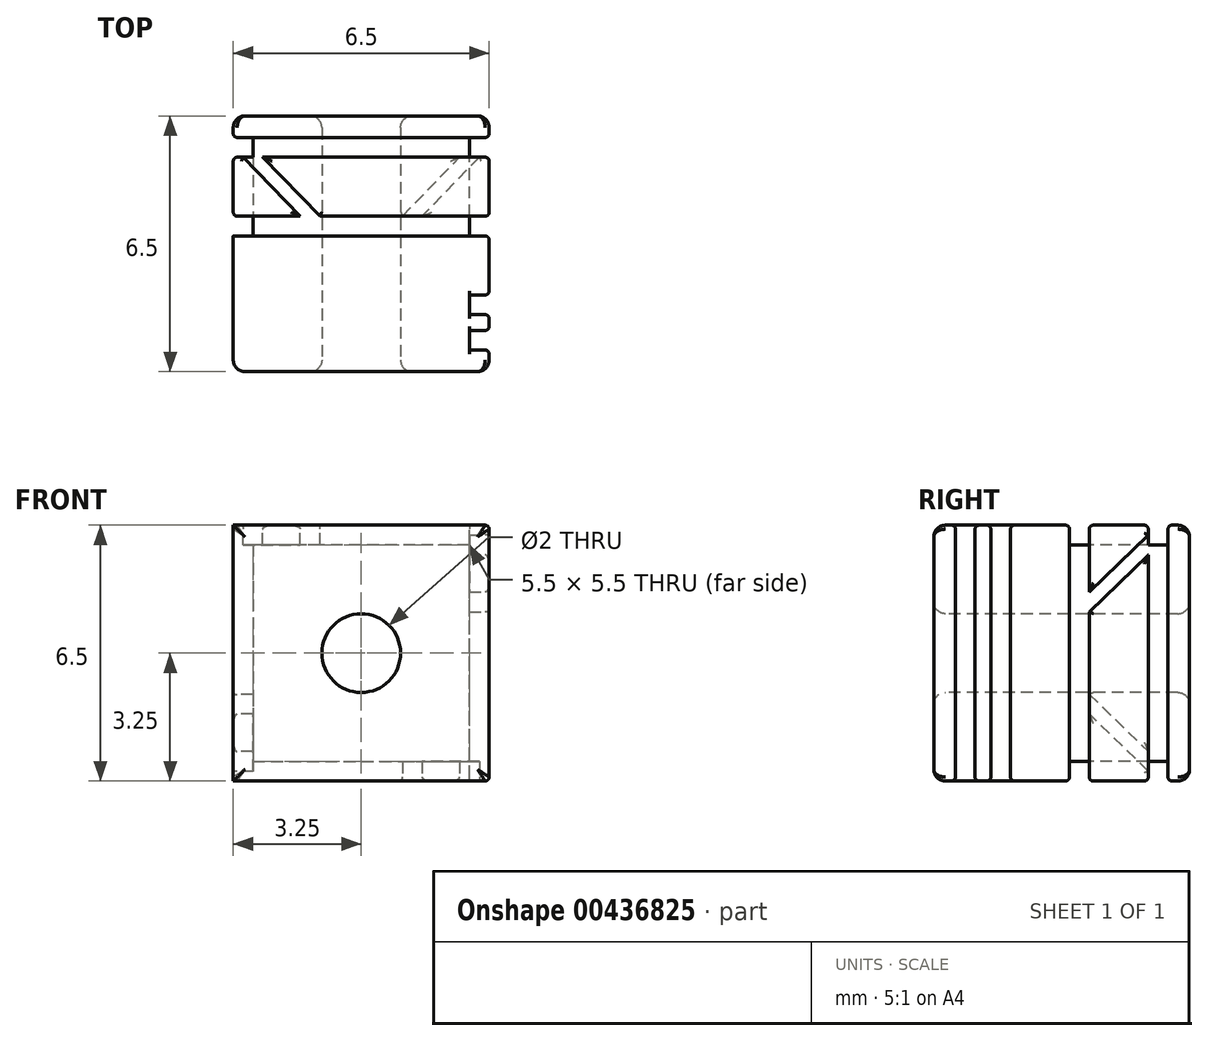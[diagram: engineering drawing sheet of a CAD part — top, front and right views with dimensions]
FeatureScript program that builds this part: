
annotation { "Feature Type Name" : "Feature", "Feature Type Description" : "" }
export const myFeature = defineFeature(function(context is Context, id is Id, definition is map)
    precondition{}
    {
        {
            var Q0;
            Q0=qCreatedBy(makeId("Front.planeOp"),FACE);
            var sketch = newSketch(context, id + "F0", { "sketchPlane" : qUnion([Q0])});
            skLineSegment(sketch, "E0.bottom", {"start": v(0, 0) * mm, "end": v(6.5, 0) * mm});
            skLineSegment(sketch, "E0.top", {"start": v(0, -6.5) * mm, "end": v(6.5, -6.5) * mm});
            skLineSegment(sketch, "E0.left", {"start": v(0, 0) * mm, "end": v(0, -6.5) * mm});
            skLineSegment(sketch, "E0.right", {"start": v(6.5, 0) * mm, "end": v(6.5, -6.5) * mm});
            skSolve(sketch);
        }
        {
            var Q0;
            Q0=makeQuery(id+"F0.imprint","IMPRINT",FACE,{"disambiguationData":[TD([[makeQuery(id+"F0.imprint","IMPRINT",EDGE,{"derivedFrom":sQuery(id+"F0.wireOp",EDGE,"E0.bottom")}),-1.0]])]});
            extrude(context, id + "F1", {"entities" : qUnion([Q0]), "depth" : 6.5 * mm});
        }
        {
            var Q0;
            Q0=makeQuery(id+"F1.opExtrude","CAP_FACE",FACE,{"disambiguationData":[OSD([sQuery(id+"F0.wireOp",EDGE,"E0.bottom"),sQuery(id+"F0.wireOp",EDGE,"E0.top"),sQuery(id+"F0.wireOp",EDGE,"E0.left"),sQuery(id+"F0.wireOp",EDGE,"E0.right")])],"isStart":false});
            var sketch = newSketch(context, id + "F2", { "sketchPlane" : qUnion([Q0])});
            skCircle(sketch, "E1", {"center": v(3.25, -3.25) * mm, "radius": 1 * mm});
            skPoint(sketch, "E1.centerSnap0", {"position": v(3.25, -6.5) * mm});
            skPoint(sketch, "E1.centerSnap1", {"position": v(0, -3.25) * mm});
            skSolve(sketch);
        }
        {
            var Q0;
            Q0=makeQuery(id+"F2.imprint","IMPRINT",FACE,{"disambiguationData":[TD([[makeQuery(id+"F2.imprint","IMPRINT",EDGE,{"derivedFrom":sQuery(id+"F2.wireOp",EDGE,"E1")}),1.0]])]});
            extrude(context, id + "F3", {"entities" : qUnion([Q0]), "operationType" : NewBodyOperationType.REMOVE, "oppositeDirection" : true, "depth" : 25 * mm});
        }
        {
            var Q0;
            Q0=makeQuery(id+"F1.opExtrude","SWEPT_FACE",FACE,{"disambiguationData":[OSD([sQuery(id+"F0.wireOp",EDGE,"E0.right")])]});
            var sketch = newSketch(context, id + "F4", { "sketchPlane" : qUnion([Q0])});
            skLineSegment(sketch, "E2", {"start": v(-5.95, -6.5) * mm, "end": v(-5.95, 0) * mm});
            skLineSegment(sketch, "E3", {"start": v(-0.55, -6.5) * mm, "end": v(-0.55, 0) * mm});
            skLineSegment(sketch, "E4.bottom", {"start": v(-5.45, -6.5) * mm, "end": v(-5.05, -6.5) * mm});
            skLineSegment(sketch, "E4.top", {"start": v(-5.45, 0) * mm, "end": v(-5.05, 0) * mm});
            skLineSegment(sketch, "E4.left", {"start": v(-5.45, -6.5) * mm, "end": v(-5.45, 0) * mm});
            skLineSegment(sketch, "E4.right", {"start": v(-5.05, -6.5) * mm, "end": v(-5.05, 0) * mm});
            skLineSegment(sketch, "E5.bottom", {"start": v(-4.55, -6.5) * mm, "end": v(-3.05, -6.5) * mm});
            skLineSegment(sketch, "E5.top", {"start": v(-4.55, 0) * mm, "end": v(-3.05, 0) * mm});
            skLineSegment(sketch, "E5.left", {"start": v(-4.55, -6.5) * mm, "end": v(-4.55, 0) * mm});
            skLineSegment(sketch, "E5.right", {"start": v(-3.05, -6.5) * mm, "end": v(-3.05, 0) * mm});
            skLineSegment(sketch, "E6.bottom", {"start": v(-2.55, -6.5) * mm, "end": v(-1.05, -6.5) * mm});
            skLineSegment(sketch, "E6.top", {"start": v(-2.55, 0) * mm, "end": v(-1.05, 0) * mm});
            skLineSegment(sketch, "E6.left", {"start": v(-2.55, -6.5) * mm, "end": v(-2.55, -2.2) * mm});
            skLineSegment(sketch, "E6.right", {"start": v(-1.05, -6.5) * mm, "end": v(-1.05, -0.75) * mm});
            skLineSegment(sketch, "E7", {"start": v(-1.05, -0.25) * mm, "end": v(-2.55, -1.7) * mm});
            skLineSegment(sketch, "E8", {"start": v(-2.55, -2.2) * mm, "end": v(-1.05, -0.75) * mm});
            skLineSegment(sketch, "E9.trimOffspring", {"start": v(-2.55, -1.7) * mm, "end": v(-2.55, 0) * mm});
            skLineSegment(sketch, "E10.trimOffspring", {"start": v(-1.05, -0.25) * mm, "end": v(-1.05, 0) * mm});
            skSolve(sketch);
        }
        {
            var Q0;
            {var subQ0=sQuery(id+"F4.wireOp",EDGE,"E2");Q0=makeQuery(id+"F4.imprint","IMPRINT",FACE,{"disambiguationData":[TD([[makeQuery(id+"F4.imprint","IMPRINT",EDGE,{"derivedFrom":subQ0}),-1.0]])]});}
            var Q1;
            {var subQ0=sQuery(id+"F4.wireOp",EDGE,"E4.right");Q1=makeQuery(id+"F4.imprint","IMPRINT",FACE,{"disambiguationData":[TD([[makeQuery(id+"F4.imprint","IMPRINT",EDGE,{"derivedFrom":subQ0}),-1.0]])]});}
            var Q2;
            {var subQ6=sQuery(id+"F4.wireOp",EDGE,"E3");Q2=makeQuery(id+"F4.imprint","IMPRINT",FACE,{"disambiguationData":[TD([[makeQuery(id+"F4.imprint","IMPRINT",EDGE,{"derivedFrom":subQ6}),1.0]])]});}
            extrude(context, id + "F5", {"entities" : qUnion([Q0, Q1, Q2]), "operationType" : NewBodyOperationType.REMOVE, "oppositeDirection" : true, "depth" : 0.5 * mm, "offsetDistance" : 25 * mm});
        }
        {
            var Q0;
            Q0=makeQuery(id+"F1.opExtrude","SWEPT_FACE",FACE,{"disambiguationData":[OSD([sQuery(id+"F0.wireOp",EDGE,"E0.bottom")])]});
            var sketch = newSketch(context, id + "F6", { "sketchPlane" : qUnion([Q0])});
            skLineSegment(sketch, "E11", {"start": v(6.5, -5.95) * mm, "end": v(0, -5.95) * mm});
            skLineSegment(sketch, "E12", {"start": v(6.5, -0.55) * mm, "end": v(0, -0.55) * mm});
            skLineSegment(sketch, "E13.bottom", {"start": v(6.5, -5.45) * mm, "end": v(6.5, -5.05) * mm});
            skLineSegment(sketch, "E13.top", {"start": v(0, -5.45) * mm, "end": v(0, -5.05) * mm});
            skLineSegment(sketch, "E13.left", {"start": v(6.5, -5.45) * mm, "end": v(0, -5.45) * mm});
            skLineSegment(sketch, "E13.right", {"start": v(6.5, -5.05) * mm, "end": v(0, -5.05) * mm});
            skLineSegment(sketch, "E14.bottom", {"start": v(6.5, -4.55) * mm, "end": v(6.5, -3.05) * mm});
            skLineSegment(sketch, "E14.top", {"start": v(0, -4.55) * mm, "end": v(0, -3.05) * mm});
            skLineSegment(sketch, "E14.left", {"start": v(6.5, -4.55) * mm, "end": v(0, -4.55) * mm});
            skLineSegment(sketch, "E14.right", {"start": v(6.5, -3.05) * mm, "end": v(0, -3.05) * mm});
            skLineSegment(sketch, "E15.bottom", {"start": v(6.5, -2.55) * mm, "end": v(6.5, -1.05) * mm});
            skLineSegment(sketch, "E15.top", {"start": v(0, -2.55) * mm, "end": v(0, -1.05) * mm});
            skLineSegment(sketch, "E15.left", {"start": v(6.5, -2.55) * mm, "end": v(2.2, -2.55) * mm});
            skLineSegment(sketch, "E15.right", {"start": v(6.5, -1.05) * mm, "end": v(0.75, -1.05) * mm});
            skLineSegment(sketch, "E16", {"start": v(0.25, -1.05) * mm, "end": v(1.7, -2.55) * mm});
            skLineSegment(sketch, "E17", {"start": v(2.2, -2.55) * mm, "end": v(0.75, -1.05) * mm});
            skLineSegment(sketch, "E18.trimOffspring", {"start": v(1.7, -2.55) * mm, "end": v(0, -2.55) * mm});
            skLineSegment(sketch, "E19.trimOffspring", {"start": v(0.25, -1.05) * mm, "end": v(0, -1.05) * mm});
            skSolve(sketch);
        }
        {
            var Q0;
            {var subQ1=sQuery(id+"F0.wireOp",EDGE,"E0.right");var subQ2=sQuery(id+"F0.wireOp",EDGE,"E0.bottom");var subQ3=makeQuery(id+"F1.opExtrude","SWEPT_EDGE",EDGE,{"disambiguationData":[OSD([subQ2,subQ1])]});var subQ4=makeQuery(id+"F5.boolean.opBoolean","COPY",EDGE,{"derivedFrom":makeQuery(id+"F5.opExtrude","CAP_EDGE",EDGE,{"disambiguationData":[OSD([subQ2,subQ1]),TDD([makeQuery(id+"F4.imprint","IMPRINT",EDGE,{"disambiguationData":[TD([[makeQuery(id+"F4.imprint","INTERSECT",VERTEX,{"derivedFrom":[subQ3,sQuery(id+"F4.wireOp",EDGE,"E2")]}),-1.0]])],"derivedFrom":subQ3})])],"isStart":false})});Q0=makeQuery(id+"F6.imprint","IMPRINT",FACE,{"disambiguationData":[TD([[makeQuery(id+"F6.imprint","IMPRINT",EDGE,{"derivedFrom":subQ4}),1.0]])]});}
            var Q1;
            {var subQ1=sQuery(id+"F0.wireOp",EDGE,"E0.right");var subQ2=sQuery(id+"F0.wireOp",EDGE,"E0.bottom");var subQ3=makeQuery(id+"F1.opExtrude","SWEPT_EDGE",EDGE,{"disambiguationData":[OSD([subQ2,subQ1])]});var subQ4=makeQuery(id+"F5.boolean.opBoolean","COPY",EDGE,{"derivedFrom":makeQuery(id+"F5.opExtrude","CAP_EDGE",EDGE,{"disambiguationData":[OSD([subQ2,subQ1]),TDD([makeQuery(id+"F4.imprint","IMPRINT",EDGE,{"disambiguationData":[TD([[makeQuery(id+"F4.imprint","INTERSECT",VERTEX,{"derivedFrom":[subQ3,sQuery(id+"F4.wireOp",EDGE,"E4.top"),sQuery(id+"F4.wireOp",EDGE,"E4.right")]}),-1.0]])],"derivedFrom":subQ3})])],"isStart":false})});Q1=makeQuery(id+"F6.imprint","IMPRINT",FACE,{"disambiguationData":[TD([[makeQuery(id+"F6.imprint","IMPRINT",EDGE,{"derivedFrom":subQ4}),1.0]])]});}
            var Q2;
            Q2=makeQuery(id+"F6.imprint","IMPRINT",FACE,{"disambiguationData":[TD([[makeQuery(id+"F6.imprint","IMPRINT",EDGE,{"derivedFrom":sQuery(id+"F6.wireOp",EDGE,"E16")}),1.0]])]});
            extrude(context, id + "F7", {"entities" : qUnion([Q0, Q1, Q2]), "operationType" : NewBodyOperationType.REMOVE, "oppositeDirection" : true, "depth" : 0.5 * mm, "offsetDistance" : 25 * mm});
        }
        {
            var Q0;
            Q0=makeQuery(id+"F1.opExtrude","SWEPT_FACE",FACE,{"disambiguationData":[OSD([sQuery(id+"F0.wireOp",EDGE,"E0.left")])]});
            var sketch = newSketch(context, id + "F8", { "sketchPlane" : qUnion([Q0])});
            skLineSegment(sketch, "E20", {"start": v(5.95, 0) * mm, "end": v(5.95, -6.5) * mm});
            skLineSegment(sketch, "E21", {"start": v(0.55, 0) * mm, "end": v(0.55, -6.5) * mm});
            skLineSegment(sketch, "E22.bottom", {"start": v(5.45, 0) * mm, "end": v(5.05, 0) * mm});
            skLineSegment(sketch, "E22.top", {"start": v(5.45, -6.5) * mm, "end": v(5.05, -6.5) * mm});
            skLineSegment(sketch, "E22.left", {"start": v(5.45, 0) * mm, "end": v(5.45, -6.5) * mm});
            skLineSegment(sketch, "E22.right", {"start": v(5.05, 0) * mm, "end": v(5.05, -6.5) * mm});
            skLineSegment(sketch, "E23.bottom", {"start": v(4.55, 0) * mm, "end": v(3.05, 0) * mm});
            skLineSegment(sketch, "E23.top", {"start": v(4.55, -6.5) * mm, "end": v(3.05, -6.5) * mm});
            skLineSegment(sketch, "E23.left", {"start": v(4.55, 0) * mm, "end": v(4.55, -6.5) * mm});
            skLineSegment(sketch, "E23.right", {"start": v(3.05, 0) * mm, "end": v(3.05, -6.5) * mm});
            skLineSegment(sketch, "E24.bottom", {"start": v(2.55, 0) * mm, "end": v(1.05, 0) * mm});
            skLineSegment(sketch, "E24.top", {"start": v(2.55, -6.5) * mm, "end": v(1.05, -6.5) * mm});
            skLineSegment(sketch, "E24.left", {"start": v(2.55, 0) * mm, "end": v(2.55, -4.3) * mm});
            skLineSegment(sketch, "E24.right", {"start": v(1.05, 0) * mm, "end": v(1.05, -5.75) * mm});
            skLineSegment(sketch, "E25", {"start": v(1.05, -6.25) * mm, "end": v(2.55, -4.8) * mm});
            skLineSegment(sketch, "E26", {"start": v(2.55, -4.3) * mm, "end": v(1.05, -5.75) * mm});
            skLineSegment(sketch, "E27.trimOffspring", {"start": v(2.55, -4.8) * mm, "end": v(2.55, -6.5) * mm});
            skLineSegment(sketch, "E28.trimOffspring", {"start": v(1.05, -6.25) * mm, "end": v(1.05, -6.5) * mm});
            skSolve(sketch);
        }
        {
            var Q0;
            {var subQ1=sQuery(id+"F0.wireOp",EDGE,"E0.left");var subQ2=sQuery(id+"F0.wireOp",EDGE,"E0.bottom");var subQ3=makeQuery(id+"F1.opExtrude","SWEPT_EDGE",EDGE,{"disambiguationData":[OSD([subQ2,subQ1])]});var subQ4=makeQuery(id+"F7.boolean.opBoolean","COPY",EDGE,{"derivedFrom":makeQuery(id+"F7.opExtrude","CAP_EDGE",EDGE,{"disambiguationData":[OSD([subQ2,subQ1]),TDD([makeQuery(id+"F6.imprint","IMPRINT",EDGE,{"disambiguationData":[TD([[makeQuery(id+"F6.imprint","INTERSECT",VERTEX,{"derivedFrom":[subQ3,sQuery(id+"F6.wireOp",EDGE,"E11")]}),-1.0]])],"derivedFrom":subQ3})])],"isStart":false})});Q0=makeQuery(id+"F8.imprint","IMPRINT",FACE,{"disambiguationData":[TD([[makeQuery(id+"F8.imprint","IMPRINT",EDGE,{"derivedFrom":subQ4}),1.0]])]});}
            var Q1;
            {var subQ1=sQuery(id+"F0.wireOp",EDGE,"E0.left");var subQ2=sQuery(id+"F0.wireOp",EDGE,"E0.bottom");var subQ3=makeQuery(id+"F1.opExtrude","SWEPT_EDGE",EDGE,{"disambiguationData":[OSD([subQ2,subQ1])]});var subQ4=makeQuery(id+"F7.boolean.opBoolean","COPY",EDGE,{"derivedFrom":makeQuery(id+"F7.opExtrude","CAP_EDGE",EDGE,{"disambiguationData":[OSD([subQ2,subQ1]),TDD([makeQuery(id+"F6.imprint","IMPRINT",EDGE,{"disambiguationData":[TD([[makeQuery(id+"F6.imprint","INTERSECT",VERTEX,{"derivedFrom":[subQ3,sQuery(id+"F6.wireOp",EDGE,"E13.top"),sQuery(id+"F6.wireOp",EDGE,"E13.right")]}),-1.0]])],"derivedFrom":subQ3})])],"isStart":false})});Q1=makeQuery(id+"F8.imprint","IMPRINT",FACE,{"disambiguationData":[TD([[makeQuery(id+"F8.imprint","IMPRINT",EDGE,{"derivedFrom":subQ4}),1.0]])]});}
            var Q2;
            Q2=makeQuery(id+"F8.imprint","IMPRINT",FACE,{"disambiguationData":[TD([[makeQuery(id+"F8.imprint","IMPRINT",EDGE,{"derivedFrom":sQuery(id+"F8.wireOp",EDGE,"E25")}),1.0]])]});
            extrude(context, id + "F9", {"entities" : qUnion([Q0, Q1, Q2]), "operationType" : NewBodyOperationType.REMOVE, "oppositeDirection" : true, "depth" : 0.5 * mm, "offsetDistance" : 25 * mm});
        }
        {
            var Q0;
            Q0=makeQuery(id+"F1.opExtrude","SWEPT_FACE",FACE,{"disambiguationData":[OSD([sQuery(id+"F0.wireOp",EDGE,"E0.top")])]});
            var sketch = newSketch(context, id + "F10", { "sketchPlane" : qUnion([Q0])});
            skLineSegment(sketch, "E29", {"start": v(0, 5.95) * mm, "end": v(6.5, 5.95) * mm});
            skLineSegment(sketch, "E30", {"start": v(0, 0.55) * mm, "end": v(6.5, 0.55) * mm});
            skLineSegment(sketch, "E31.bottom", {"start": v(0, 5.45) * mm, "end": v(0, 5.05) * mm});
            skLineSegment(sketch, "E31.top", {"start": v(6.5, 5.45) * mm, "end": v(6.5, 5.05) * mm});
            skLineSegment(sketch, "E31.left", {"start": v(0, 5.45) * mm, "end": v(6.5, 5.45) * mm});
            skLineSegment(sketch, "E31.right", {"start": v(0, 5.05) * mm, "end": v(6.5, 5.05) * mm});
            skLineSegment(sketch, "E32.bottom", {"start": v(0, 4.55) * mm, "end": v(0, 3.05) * mm});
            skLineSegment(sketch, "E32.top", {"start": v(6.5, 4.55) * mm, "end": v(6.5, 3.05) * mm});
            skLineSegment(sketch, "E32.left", {"start": v(0, 4.55) * mm, "end": v(6.5, 4.55) * mm});
            skLineSegment(sketch, "E32.right", {"start": v(0, 3.05) * mm, "end": v(6.5, 3.05) * mm});
            skLineSegment(sketch, "E33.bottom", {"start": v(0, 2.55) * mm, "end": v(0, 1.05) * mm});
            skLineSegment(sketch, "E33.top", {"start": v(6.5, 2.55) * mm, "end": v(6.5, 1.05) * mm});
            skLineSegment(sketch, "E33.left", {"start": v(0, 2.55) * mm, "end": v(4.3, 2.55) * mm});
            skLineSegment(sketch, "E33.right", {"start": v(0, 1.05) * mm, "end": v(5.75, 1.05) * mm});
            skLineSegment(sketch, "E34", {"start": v(6.25, 1.05) * mm, "end": v(4.8, 2.55) * mm});
            skLineSegment(sketch, "E35", {"start": v(4.3, 2.55) * mm, "end": v(5.75, 1.05) * mm});
            skLineSegment(sketch, "E36.trimOffspring", {"start": v(4.8, 2.55) * mm, "end": v(6.5, 2.55) * mm});
            skLineSegment(sketch, "E37.trimOffspring", {"start": v(6.25, 1.05) * mm, "end": v(6.5, 1.05) * mm});
            skSolve(sketch);
        }
        {
            var Q0;
            {var subQ1=sQuery(id+"F0.wireOp",EDGE,"E0.right");var subQ2=sQuery(id+"F0.wireOp",EDGE,"E0.top");var subQ3=makeQuery(id+"F1.opExtrude","SWEPT_EDGE",EDGE,{"disambiguationData":[OSD([subQ2,subQ1])]});var subQ4=makeQuery(id+"F5.boolean.opBoolean","COPY",EDGE,{"derivedFrom":makeQuery(id+"F5.opExtrude","CAP_EDGE",EDGE,{"disambiguationData":[OSD([subQ2,subQ1]),TDD([makeQuery(id+"F4.imprint","IMPRINT",EDGE,{"disambiguationData":[TD([[makeQuery(id+"F4.imprint","INTERSECT",VERTEX,{"derivedFrom":[subQ3,sQuery(id+"F4.wireOp",EDGE,"E2")]}),-1.0]])],"derivedFrom":subQ3})])],"isStart":false})});Q0=makeQuery(id+"F10.imprint","IMPRINT",FACE,{"disambiguationData":[TD([[makeQuery(id+"F10.imprint","IMPRINT",EDGE,{"derivedFrom":subQ4}),-1.0]])]});}
            var Q1;
            {var subQ1=sQuery(id+"F0.wireOp",EDGE,"E0.right");var subQ2=sQuery(id+"F0.wireOp",EDGE,"E0.top");var subQ3=makeQuery(id+"F1.opExtrude","SWEPT_EDGE",EDGE,{"disambiguationData":[OSD([subQ2,subQ1])]});var subQ4=makeQuery(id+"F5.boolean.opBoolean","COPY",EDGE,{"derivedFrom":makeQuery(id+"F5.opExtrude","CAP_EDGE",EDGE,{"disambiguationData":[OSD([subQ2,subQ1]),TDD([makeQuery(id+"F4.imprint","IMPRINT",EDGE,{"disambiguationData":[TD([[makeQuery(id+"F4.imprint","INTERSECT",VERTEX,{"derivedFrom":[subQ3,sQuery(id+"F4.wireOp",EDGE,"E4.bottom"),sQuery(id+"F4.wireOp",EDGE,"E4.right")]}),-1.0]])],"derivedFrom":subQ3})])],"isStart":false})});Q1=makeQuery(id+"F10.imprint","IMPRINT",FACE,{"disambiguationData":[TD([[makeQuery(id+"F10.imprint","IMPRINT",EDGE,{"derivedFrom":subQ4}),-1.0]])]});}
            var Q2;
            {var subQ6=sQuery(id+"F10.wireOp",EDGE,"E34");Q2=makeQuery(id+"F10.imprint","IMPRINT",FACE,{"disambiguationData":[TD([[makeQuery(id+"F10.imprint","IMPRINT",EDGE,{"derivedFrom":subQ6}),1.0]])]});}
            extrude(context, id + "F11", {"entities" : qUnion([Q0, Q1, Q2]), "operationType" : NewBodyOperationType.REMOVE, "oppositeDirection" : true, "depth" : 0.5 * mm, "offsetDistance" : 25 * mm});
        }
        {
            var Q0;
            {var subQ0=sQuery(id+"F0.wireOp",EDGE,"E0.left");var subQ1=sQuery(id+"F0.wireOp",EDGE,"E0.bottom");Q0=makeQuery(id+"F7.boolean.opBoolean","SPLIT",EDGE,{"disambiguationData":[TD([makeQuery(id+"F5.boolean.opBoolean","COPY",FACE,{"derivedFrom":makeQuery(id+"F5.opExtrude","SWEPT_FACE",FACE,{"disambiguationData":[OSD([sQuery(id+"F4.wireOp",EDGE,"E2")])]})})])],"derivedFrom":makeQuery(id+"F1.opExtrude","SWEPT_EDGE",EDGE,{"disambiguationData":[OSD([subQ1,subQ0])]})});}
            var Q1;
            {var subQ0=sQuery(id+"F0.wireOp",EDGE,"E0.left");var subQ1=sQuery(id+"F0.wireOp",EDGE,"E0.bottom");var subQ2=makeQuery(id+"F1.opExtrude","SWEPT_EDGE",EDGE,{"disambiguationData":[OSD([subQ1,subQ0])]});Q1=makeQuery(id+"F9.boolean.opBoolean","COPY",EDGE,{"derivedFrom":makeQuery(id+"F9.opExtrude","CAP_EDGE",EDGE,{"disambiguationData":[OSD([subQ1,subQ0]),TDD([makeQuery(id+"F8.imprint","IMPRINT",EDGE,{"derivedFrom":makeQuery(id+"F7.boolean.opBoolean","COPY",EDGE,{"derivedFrom":makeQuery(id+"F7.opExtrude","CAP_EDGE",EDGE,{"disambiguationData":[OSD([subQ1,subQ0]),TDD([makeQuery(id+"F6.imprint","IMPRINT",EDGE,{"disambiguationData":[TD([[makeQuery(id+"F6.imprint","INTERSECT",VERTEX,{"derivedFrom":[subQ2,sQuery(id+"F6.wireOp",EDGE,"E11")]}),-1.0]])],"derivedFrom":subQ2})])],"isStart":false})})})])],"isStart":false})});}
            var Q2;
            {var subQ0=sQuery(id+"F0.wireOp",EDGE,"E0.left");var subQ1=sQuery(id+"F0.wireOp",EDGE,"E0.bottom");Q2=makeQuery(id+"F7.boolean.opBoolean","SPLIT",EDGE,{"disambiguationData":[TD([makeQuery(id+"F5.boolean.opBoolean","COPY",FACE,{"derivedFrom":makeQuery(id+"F5.opExtrude","SWEPT_FACE",FACE,{"disambiguationData":[OSD([sQuery(id+"F4.wireOp",EDGE,"E4.left")])]})})])],"derivedFrom":makeQuery(id+"F1.opExtrude","SWEPT_EDGE",EDGE,{"disambiguationData":[OSD([subQ1,subQ0])]})});}
            var Q3;
            {var subQ0=sQuery(id+"F0.wireOp",EDGE,"E0.left");var subQ1=sQuery(id+"F0.wireOp",EDGE,"E0.bottom");var subQ2=makeQuery(id+"F1.opExtrude","SWEPT_EDGE",EDGE,{"disambiguationData":[OSD([subQ1,subQ0])]});Q3=makeQuery(id+"F9.boolean.opBoolean","COPY",EDGE,{"derivedFrom":makeQuery(id+"F9.opExtrude","CAP_EDGE",EDGE,{"disambiguationData":[OSD([subQ1,subQ0]),TDD([makeQuery(id+"F8.imprint","IMPRINT",EDGE,{"derivedFrom":makeQuery(id+"F7.boolean.opBoolean","COPY",EDGE,{"derivedFrom":makeQuery(id+"F7.opExtrude","CAP_EDGE",EDGE,{"disambiguationData":[OSD([subQ1,subQ0]),TDD([makeQuery(id+"F6.imprint","IMPRINT",EDGE,{"disambiguationData":[TD([[makeQuery(id+"F6.imprint","INTERSECT",VERTEX,{"derivedFrom":[subQ2,sQuery(id+"F6.wireOp",EDGE,"E13.top"),sQuery(id+"F6.wireOp",EDGE,"E13.right")]}),-1.0]])],"derivedFrom":subQ2})])],"isStart":false})})})])],"isStart":false})});}
            var Q4;
            {var subQ0=sQuery(id+"F0.wireOp",EDGE,"E0.left");var subQ1=sQuery(id+"F0.wireOp",EDGE,"E0.bottom");Q4=makeQuery(id+"F7.boolean.opBoolean","SPLIT",EDGE,{"disambiguationData":[TD([makeQuery(id+"F5.boolean.opBoolean","COPY",FACE,{"derivedFrom":makeQuery(id+"F5.opExtrude","SWEPT_FACE",FACE,{"disambiguationData":[OSD([sQuery(id+"F4.wireOp",EDGE,"E5.left")])]})})])],"derivedFrom":makeQuery(id+"F1.opExtrude","SWEPT_EDGE",EDGE,{"disambiguationData":[OSD([subQ1,subQ0])]})});}
            var Q5;
            {var subQ0=sQuery(id+"F0.wireOp",EDGE,"E0.left");var subQ1=sQuery(id+"F0.wireOp",EDGE,"E0.bottom");var subQ2=makeQuery(id+"F1.opExtrude","SWEPT_EDGE",EDGE,{"disambiguationData":[OSD([subQ1,subQ0])]});Q5=makeQuery(id+"F9.boolean.opBoolean","COPY",EDGE,{"derivedFrom":makeQuery(id+"F9.opExtrude","CAP_EDGE",EDGE,{"disambiguationData":[OSD([subQ1,subQ0]),TDD([makeQuery(id+"F8.imprint","IMPRINT",EDGE,{"derivedFrom":makeQuery(id+"F7.boolean.opBoolean","COPY",EDGE,{"derivedFrom":makeQuery(id+"F7.opExtrude","CAP_EDGE",EDGE,{"disambiguationData":[OSD([subQ1,subQ0]),TDD([makeQuery(id+"F6.imprint","IMPRINT",EDGE,{"disambiguationData":[TD([[makeQuery(id+"F6.imprint","INTERSECT",VERTEX,{"derivedFrom":[subQ2,sQuery(id+"F6.wireOp",EDGE,"E14.top"),sQuery(id+"F6.wireOp",EDGE,"E14.right")]}),-1.0]])],"derivedFrom":subQ2})])],"isStart":false})})})])],"isStart":false})});}
            var Q6;
            {var subQ0=sQuery(id+"F0.wireOp",EDGE,"E0.bottom");var subQ1=sQuery(id+"F0.wireOp",EDGE,"E0.left");Q6=makeQuery(id+"F7.boolean.opBoolean","SPLIT",EDGE,{"disambiguationData":[TD([makeQuery(id+"F7.opExtrude","SWEPT_FACE",FACE,{"disambiguationData":[OSD([sQuery(id+"F6.wireOp",EDGE,"E18.trimOffspring")])]})])],"derivedFrom":makeQuery(id+"F1.opExtrude","SWEPT_EDGE",EDGE,{"disambiguationData":[OSD([subQ0,subQ1])]})});}
            var Q7;
            {var subQ0=sQuery(id+"F0.wireOp",EDGE,"E0.left");var subQ1=sQuery(id+"F0.wireOp",EDGE,"E0.bottom");var subQ2=makeQuery(id+"F1.opExtrude","SWEPT_EDGE",EDGE,{"disambiguationData":[OSD([subQ1,subQ0])]});Q7=makeQuery(id+"F9.boolean.opBoolean","COPY",EDGE,{"derivedFrom":makeQuery(id+"F9.opExtrude","CAP_EDGE",EDGE,{"disambiguationData":[OSD([subQ1,subQ0]),TDD([makeQuery(id+"F8.imprint","IMPRINT",EDGE,{"derivedFrom":makeQuery(id+"F7.boolean.opBoolean","COPY",EDGE,{"derivedFrom":makeQuery(id+"F7.opExtrude","CAP_EDGE",EDGE,{"disambiguationData":[OSD([subQ1,subQ0]),TDD([makeQuery(id+"F6.imprint","IMPRINT",EDGE,{"disambiguationData":[TD([[makeQuery(id+"F6.imprint","INTERSECT",VERTEX,{"derivedFrom":[subQ2,sQuery(id+"F6.wireOp",EDGE,"E12")]}),1.0]])],"derivedFrom":subQ2})])],"isStart":false})})})])],"isStart":false})});}
            var Q8;
            {var subQ0=sQuery(id+"F0.wireOp",EDGE,"E0.left");var subQ1=sQuery(id+"F0.wireOp",EDGE,"E0.bottom");Q8=makeQuery(id+"F7.boolean.opBoolean","SPLIT",EDGE,{"disambiguationData":[TD([makeQuery(id+"F5.boolean.opBoolean","COPY",FACE,{"derivedFrom":makeQuery(id+"F5.opExtrude","SWEPT_FACE",FACE,{"disambiguationData":[OSD([sQuery(id+"F4.wireOp",EDGE,"E3")])]})})])],"derivedFrom":makeQuery(id+"F1.opExtrude","SWEPT_EDGE",EDGE,{"disambiguationData":[OSD([subQ1,subQ0])]})});}
            var Q9;
            {var subQ0=sQuery(id+"F0.wireOp",EDGE,"E0.left");var subQ1=sQuery(id+"F0.wireOp",EDGE,"E0.top");Q9=makeQuery(id+"F9.boolean.opBoolean","SPLIT",EDGE,{"disambiguationData":[TD([makeQuery(id+"F5.boolean.opBoolean","COPY",FACE,{"derivedFrom":makeQuery(id+"F5.opExtrude","SWEPT_FACE",FACE,{"disambiguationData":[OSD([sQuery(id+"F4.wireOp",EDGE,"E2")])]})})])],"derivedFrom":makeQuery(id+"F1.opExtrude","SWEPT_EDGE",EDGE,{"disambiguationData":[OSD([subQ1,subQ0])]})});}
            var Q10;
            {var subQ0=sQuery(id+"F0.wireOp",EDGE,"E0.left");var subQ1=sQuery(id+"F0.wireOp",EDGE,"E0.top");var subQ2=makeQuery(id+"F1.opExtrude","SWEPT_EDGE",EDGE,{"disambiguationData":[OSD([subQ1,subQ0])]});Q10=makeQuery(id+"F11.boolean.opBoolean","COPY",EDGE,{"derivedFrom":makeQuery(id+"F11.opExtrude","CAP_EDGE",EDGE,{"disambiguationData":[OSD([subQ1,subQ0]),TDD([makeQuery(id+"F10.imprint","IMPRINT",EDGE,{"derivedFrom":makeQuery(id+"F9.boolean.opBoolean","COPY",EDGE,{"derivedFrom":makeQuery(id+"F9.opExtrude","CAP_EDGE",EDGE,{"disambiguationData":[OSD([subQ1,subQ0]),TDD([makeQuery(id+"F8.imprint","IMPRINT",EDGE,{"disambiguationData":[TD([[makeQuery(id+"F8.imprint","INTERSECT",VERTEX,{"derivedFrom":[subQ2,sQuery(id+"F8.wireOp",EDGE,"E20")]}),-1.0]])],"derivedFrom":subQ2})])],"isStart":false})})})])],"isStart":false})});}
            var Q11;
            {var subQ0=sQuery(id+"F0.wireOp",EDGE,"E0.top");var subQ1=sQuery(id+"F0.wireOp",EDGE,"E0.left");Q11=makeQuery(id+"F9.boolean.opBoolean","SPLIT",EDGE,{"disambiguationData":[TD([makeQuery(id+"F5.boolean.opBoolean","COPY",FACE,{"derivedFrom":makeQuery(id+"F5.opExtrude","SWEPT_FACE",FACE,{"disambiguationData":[OSD([sQuery(id+"F4.wireOp",EDGE,"E4.left")])]})})])],"derivedFrom":makeQuery(id+"F1.opExtrude","SWEPT_EDGE",EDGE,{"disambiguationData":[OSD([subQ0,subQ1])]})});}
            var Q12;
            {var subQ0=sQuery(id+"F0.wireOp",EDGE,"E0.left");var subQ1=sQuery(id+"F0.wireOp",EDGE,"E0.top");var subQ2=makeQuery(id+"F1.opExtrude","SWEPT_EDGE",EDGE,{"disambiguationData":[OSD([subQ1,subQ0])]});Q12=makeQuery(id+"F11.boolean.opBoolean","COPY",EDGE,{"derivedFrom":makeQuery(id+"F11.opExtrude","CAP_EDGE",EDGE,{"disambiguationData":[OSD([subQ1,subQ0]),TDD([makeQuery(id+"F10.imprint","IMPRINT",EDGE,{"derivedFrom":makeQuery(id+"F9.boolean.opBoolean","COPY",EDGE,{"derivedFrom":makeQuery(id+"F9.opExtrude","CAP_EDGE",EDGE,{"disambiguationData":[OSD([subQ1,subQ0]),TDD([makeQuery(id+"F8.imprint","IMPRINT",EDGE,{"disambiguationData":[TD([[makeQuery(id+"F8.imprint","INTERSECT",VERTEX,{"derivedFrom":[subQ2,sQuery(id+"F8.wireOp",EDGE,"E22.top"),sQuery(id+"F8.wireOp",EDGE,"E22.right")]}),-1.0]])],"derivedFrom":subQ2})])],"isStart":false})})})])],"isStart":false})});}
            var Q13;
            {var subQ0=sQuery(id+"F0.wireOp",EDGE,"E0.left");var subQ1=sQuery(id+"F0.wireOp",EDGE,"E0.top");Q13=makeQuery(id+"F9.boolean.opBoolean","SPLIT",EDGE,{"disambiguationData":[TD([makeQuery(id+"F5.boolean.opBoolean","COPY",FACE,{"derivedFrom":makeQuery(id+"F5.opExtrude","SWEPT_FACE",FACE,{"disambiguationData":[OSD([sQuery(id+"F4.wireOp",EDGE,"E5.left")])]})})])],"derivedFrom":makeQuery(id+"F1.opExtrude","SWEPT_EDGE",EDGE,{"disambiguationData":[OSD([subQ1,subQ0])]})});}
            var Q14;
            {var subQ0=sQuery(id+"F0.wireOp",EDGE,"E0.left");var subQ1=sQuery(id+"F0.wireOp",EDGE,"E0.top");var subQ2=makeQuery(id+"F1.opExtrude","SWEPT_EDGE",EDGE,{"disambiguationData":[OSD([subQ1,subQ0])]});Q14=makeQuery(id+"F11.boolean.opBoolean","COPY",EDGE,{"derivedFrom":makeQuery(id+"F11.opExtrude","CAP_EDGE",EDGE,{"disambiguationData":[OSD([subQ1,subQ0]),TDD([makeQuery(id+"F10.imprint","IMPRINT",EDGE,{"derivedFrom":makeQuery(id+"F9.boolean.opBoolean","COPY",EDGE,{"derivedFrom":makeQuery(id+"F9.opExtrude","CAP_EDGE",EDGE,{"disambiguationData":[OSD([subQ1,subQ0]),TDD([makeQuery(id+"F8.imprint","IMPRINT",EDGE,{"disambiguationData":[TD([[makeQuery(id+"F8.imprint","INTERSECT",VERTEX,{"derivedFrom":[subQ2,sQuery(id+"F8.wireOp",EDGE,"E23.top"),sQuery(id+"F8.wireOp",EDGE,"E23.right")]}),-1.0]])],"derivedFrom":subQ2})])],"isStart":false})})})])],"isStart":false})});}
            var Q15;
            {var subQ0=sQuery(id+"F0.wireOp",EDGE,"E0.top");var subQ1=sQuery(id+"F0.wireOp",EDGE,"E0.left");Q15=makeQuery(id+"F9.boolean.opBoolean","SPLIT",EDGE,{"disambiguationData":[TD([makeQuery(id+"F9.opExtrude","SWEPT_FACE",FACE,{"disambiguationData":[OSD([sQuery(id+"F8.wireOp",EDGE,"E27.trimOffspring")])]})])],"derivedFrom":makeQuery(id+"F1.opExtrude","SWEPT_EDGE",EDGE,{"disambiguationData":[OSD([subQ0,subQ1])]})});}
            var Q16;
            {var subQ0=sQuery(id+"F0.wireOp",EDGE,"E0.left");var subQ1=sQuery(id+"F0.wireOp",EDGE,"E0.top");var subQ2=makeQuery(id+"F1.opExtrude","SWEPT_EDGE",EDGE,{"disambiguationData":[OSD([subQ1,subQ0])]});Q16=makeQuery(id+"F11.boolean.opBoolean","COPY",EDGE,{"derivedFrom":makeQuery(id+"F11.opExtrude","CAP_EDGE",EDGE,{"disambiguationData":[OSD([subQ1,subQ0]),TDD([makeQuery(id+"F10.imprint","IMPRINT",EDGE,{"derivedFrom":makeQuery(id+"F9.boolean.opBoolean","COPY",EDGE,{"derivedFrom":makeQuery(id+"F9.opExtrude","CAP_EDGE",EDGE,{"disambiguationData":[OSD([subQ1,subQ0]),TDD([makeQuery(id+"F8.imprint","IMPRINT",EDGE,{"disambiguationData":[TD([[makeQuery(id+"F8.imprint","INTERSECT",VERTEX,{"derivedFrom":[subQ2,sQuery(id+"F8.wireOp",EDGE,"E21")]}),1.0]])],"derivedFrom":subQ2})])],"isStart":false})})})])],"isStart":false})});}
            var Q17;
            {var subQ0=sQuery(id+"F0.wireOp",EDGE,"E0.left");var subQ1=sQuery(id+"F0.wireOp",EDGE,"E0.top");Q17=makeQuery(id+"F9.boolean.opBoolean","SPLIT",EDGE,{"disambiguationData":[TD([makeQuery(id+"F5.boolean.opBoolean","COPY",FACE,{"derivedFrom":makeQuery(id+"F5.opExtrude","SWEPT_FACE",FACE,{"disambiguationData":[OSD([sQuery(id+"F4.wireOp",EDGE,"E3")])]})})])],"derivedFrom":makeQuery(id+"F1.opExtrude","SWEPT_EDGE",EDGE,{"disambiguationData":[OSD([subQ1,subQ0])]})});}
            var Q18;
            {var subQ0=sQuery(id+"F0.wireOp",EDGE,"E0.right");var subQ1=sQuery(id+"F0.wireOp",EDGE,"E0.top");Q18=makeQuery(id+"F5.boolean.opBoolean","SPLIT",EDGE,{"disambiguationData":[TD([makeQuery(id+"F5.opExtrude","SWEPT_FACE",FACE,{"disambiguationData":[OSD([sQuery(id+"F4.wireOp",EDGE,"E2")])]})])],"derivedFrom":makeQuery(id+"F1.opExtrude","SWEPT_EDGE",EDGE,{"disambiguationData":[OSD([subQ1,subQ0])]})});}
            var Q19;
            {var subQ0=sQuery(id+"F0.wireOp",EDGE,"E0.right");var subQ1=sQuery(id+"F0.wireOp",EDGE,"E0.top");var subQ2=makeQuery(id+"F1.opExtrude","SWEPT_EDGE",EDGE,{"disambiguationData":[OSD([subQ1,subQ0])]});Q19=makeQuery(id+"F11.boolean.opBoolean","COPY",EDGE,{"derivedFrom":makeQuery(id+"F11.opExtrude","CAP_EDGE",EDGE,{"disambiguationData":[OSD([subQ1,subQ0]),TDD([makeQuery(id+"F10.imprint","IMPRINT",EDGE,{"derivedFrom":makeQuery(id+"F5.boolean.opBoolean","COPY",EDGE,{"derivedFrom":makeQuery(id+"F5.opExtrude","CAP_EDGE",EDGE,{"disambiguationData":[OSD([subQ1,subQ0]),TDD([makeQuery(id+"F4.imprint","IMPRINT",EDGE,{"disambiguationData":[TD([[makeQuery(id+"F4.imprint","INTERSECT",VERTEX,{"derivedFrom":[subQ2,sQuery(id+"F4.wireOp",EDGE,"E2")]}),-1.0]])],"derivedFrom":subQ2})])],"isStart":false})})})])],"isStart":false})});}
            var Q20;
            {var subQ0=sQuery(id+"F0.wireOp",EDGE,"E0.top");var subQ1=sQuery(id+"F0.wireOp",EDGE,"E0.right");Q20=makeQuery(id+"F5.boolean.opBoolean","SPLIT",EDGE,{"disambiguationData":[TD([makeQuery(id+"F5.opExtrude","SWEPT_FACE",FACE,{"disambiguationData":[OSD([sQuery(id+"F4.wireOp",EDGE,"E4.left")])]})])],"derivedFrom":makeQuery(id+"F1.opExtrude","SWEPT_EDGE",EDGE,{"disambiguationData":[OSD([subQ0,subQ1])]})});}
            var Q21;
            {var subQ0=sQuery(id+"F0.wireOp",EDGE,"E0.right");var subQ1=sQuery(id+"F0.wireOp",EDGE,"E0.top");var subQ2=makeQuery(id+"F1.opExtrude","SWEPT_EDGE",EDGE,{"disambiguationData":[OSD([subQ1,subQ0])]});Q21=makeQuery(id+"F11.boolean.opBoolean","COPY",EDGE,{"derivedFrom":makeQuery(id+"F11.opExtrude","CAP_EDGE",EDGE,{"disambiguationData":[OSD([subQ1,subQ0]),TDD([makeQuery(id+"F10.imprint","IMPRINT",EDGE,{"derivedFrom":makeQuery(id+"F5.boolean.opBoolean","COPY",EDGE,{"derivedFrom":makeQuery(id+"F5.opExtrude","CAP_EDGE",EDGE,{"disambiguationData":[OSD([subQ1,subQ0]),TDD([makeQuery(id+"F4.imprint","IMPRINT",EDGE,{"disambiguationData":[TD([[makeQuery(id+"F4.imprint","INTERSECT",VERTEX,{"derivedFrom":[subQ2,sQuery(id+"F4.wireOp",EDGE,"E4.bottom"),sQuery(id+"F4.wireOp",EDGE,"E4.right")]}),-1.0]])],"derivedFrom":subQ2})])],"isStart":false})})})])],"isStart":false})});}
            var Q22;
            {var subQ0=sQuery(id+"F0.wireOp",EDGE,"E0.top");var subQ1=sQuery(id+"F0.wireOp",EDGE,"E0.right");Q22=makeQuery(id+"F5.boolean.opBoolean","SPLIT",EDGE,{"disambiguationData":[TD([makeQuery(id+"F5.opExtrude","SWEPT_FACE",FACE,{"disambiguationData":[OSD([sQuery(id+"F4.wireOp",EDGE,"E5.left")])]})])],"derivedFrom":makeQuery(id+"F1.opExtrude","SWEPT_EDGE",EDGE,{"disambiguationData":[OSD([subQ0,subQ1])]})});}
            var Q23;
            {var subQ0=sQuery(id+"F0.wireOp",EDGE,"E0.right");var subQ1=sQuery(id+"F0.wireOp",EDGE,"E0.top");var subQ2=makeQuery(id+"F1.opExtrude","SWEPT_EDGE",EDGE,{"disambiguationData":[OSD([subQ1,subQ0])]});Q23=makeQuery(id+"F11.boolean.opBoolean","COPY",EDGE,{"derivedFrom":makeQuery(id+"F11.opExtrude","CAP_EDGE",EDGE,{"disambiguationData":[OSD([subQ1,subQ0]),TDD([makeQuery(id+"F10.imprint","IMPRINT",EDGE,{"derivedFrom":makeQuery(id+"F5.boolean.opBoolean","COPY",EDGE,{"derivedFrom":makeQuery(id+"F5.opExtrude","CAP_EDGE",EDGE,{"disambiguationData":[OSD([subQ1,subQ0]),TDD([makeQuery(id+"F4.imprint","IMPRINT",EDGE,{"disambiguationData":[TD([[makeQuery(id+"F4.imprint","INTERSECT",VERTEX,{"derivedFrom":[subQ2,sQuery(id+"F4.wireOp",EDGE,"E5.bottom"),sQuery(id+"F4.wireOp",EDGE,"E5.right")]}),-1.0]])],"derivedFrom":subQ2})])],"isStart":false})})})])],"isStart":false})});}
            var Q24;
            {var subQ0=sQuery(id+"F0.wireOp",EDGE,"E0.top");var subQ1=sQuery(id+"F0.wireOp",EDGE,"E0.right");Q24=makeQuery(id+"F5.boolean.opBoolean","SPLIT",EDGE,{"disambiguationData":[TD([makeQuery(id+"F5.opExtrude","SWEPT_FACE",FACE,{"disambiguationData":[OSD([sQuery(id+"F4.wireOp",EDGE,"E6.left")])]})])],"derivedFrom":makeQuery(id+"F1.opExtrude","SWEPT_EDGE",EDGE,{"disambiguationData":[OSD([subQ0,subQ1])]})});}
            var Q25;
            {var subQ0=sQuery(id+"F0.wireOp",EDGE,"E0.right");var subQ1=sQuery(id+"F0.wireOp",EDGE,"E0.top");var subQ2=makeQuery(id+"F1.opExtrude","SWEPT_EDGE",EDGE,{"disambiguationData":[OSD([subQ1,subQ0])]});Q25=makeQuery(id+"F11.boolean.opBoolean","COPY",EDGE,{"derivedFrom":makeQuery(id+"F11.opExtrude","CAP_EDGE",EDGE,{"disambiguationData":[OSD([subQ1,subQ0]),TDD([makeQuery(id+"F10.imprint","IMPRINT",EDGE,{"derivedFrom":makeQuery(id+"F5.boolean.opBoolean","COPY",EDGE,{"derivedFrom":makeQuery(id+"F5.opExtrude","CAP_EDGE",EDGE,{"disambiguationData":[OSD([subQ1,subQ0]),TDD([makeQuery(id+"F4.imprint","IMPRINT",EDGE,{"disambiguationData":[TD([[makeQuery(id+"F4.imprint","INTERSECT",VERTEX,{"derivedFrom":[subQ2,sQuery(id+"F4.wireOp",EDGE,"E3")]}),1.0]])],"derivedFrom":subQ2})])],"isStart":false})})})])],"isStart":false})});}
            var Q26;
            {var subQ0=sQuery(id+"F0.wireOp",EDGE,"E0.right");var subQ1=sQuery(id+"F0.wireOp",EDGE,"E0.top");Q26=makeQuery(id+"F5.boolean.opBoolean","SPLIT",EDGE,{"disambiguationData":[TD([makeQuery(id+"F5.opExtrude","SWEPT_FACE",FACE,{"disambiguationData":[OSD([sQuery(id+"F4.wireOp",EDGE,"E3")])]})])],"derivedFrom":makeQuery(id+"F1.opExtrude","SWEPT_EDGE",EDGE,{"disambiguationData":[OSD([subQ1,subQ0])]})});}
            var Q27;
            {var subQ0=sQuery(id+"F0.wireOp",EDGE,"E0.bottom");var subQ1=sQuery(id+"F0.wireOp",EDGE,"E0.right");Q27=makeQuery(id+"F5.boolean.opBoolean","SPLIT",EDGE,{"disambiguationData":[TD([makeQuery(id+"F5.opExtrude","SWEPT_FACE",FACE,{"disambiguationData":[OSD([sQuery(id+"F4.wireOp",EDGE,"E2")])]})])],"derivedFrom":makeQuery(id+"F1.opExtrude","SWEPT_EDGE",EDGE,{"disambiguationData":[OSD([subQ0,subQ1])]})});}
            var Q28;
            {var subQ0=sQuery(id+"F0.wireOp",EDGE,"E0.right");var subQ1=sQuery(id+"F0.wireOp",EDGE,"E0.bottom");var subQ2=makeQuery(id+"F1.opExtrude","SWEPT_EDGE",EDGE,{"disambiguationData":[OSD([subQ1,subQ0])]});Q28=makeQuery(id+"F7.boolean.opBoolean","COPY",EDGE,{"derivedFrom":makeQuery(id+"F7.opExtrude","CAP_EDGE",EDGE,{"disambiguationData":[OSD([subQ1,subQ0]),TDD([makeQuery(id+"F6.imprint","IMPRINT",EDGE,{"derivedFrom":makeQuery(id+"F5.boolean.opBoolean","COPY",EDGE,{"derivedFrom":makeQuery(id+"F5.opExtrude","CAP_EDGE",EDGE,{"disambiguationData":[OSD([subQ1,subQ0]),TDD([makeQuery(id+"F4.imprint","IMPRINT",EDGE,{"disambiguationData":[TD([[makeQuery(id+"F4.imprint","INTERSECT",VERTEX,{"derivedFrom":[subQ2,sQuery(id+"F4.wireOp",EDGE,"E2")]}),-1.0]])],"derivedFrom":subQ2})])],"isStart":false})})})])],"isStart":false})});}
            var Q29;
            {var subQ0=sQuery(id+"F0.wireOp",EDGE,"E0.bottom");var subQ1=sQuery(id+"F0.wireOp",EDGE,"E0.right");Q29=makeQuery(id+"F5.boolean.opBoolean","SPLIT",EDGE,{"disambiguationData":[TD([makeQuery(id+"F5.opExtrude","SWEPT_FACE",FACE,{"disambiguationData":[OSD([sQuery(id+"F4.wireOp",EDGE,"E4.left")])]})])],"derivedFrom":makeQuery(id+"F1.opExtrude","SWEPT_EDGE",EDGE,{"disambiguationData":[OSD([subQ0,subQ1])]})});}
            var Q30;
            {var subQ0=sQuery(id+"F0.wireOp",EDGE,"E0.right");var subQ1=sQuery(id+"F0.wireOp",EDGE,"E0.bottom");var subQ2=makeQuery(id+"F1.opExtrude","SWEPT_EDGE",EDGE,{"disambiguationData":[OSD([subQ1,subQ0])]});Q30=makeQuery(id+"F7.boolean.opBoolean","COPY",EDGE,{"derivedFrom":makeQuery(id+"F7.opExtrude","CAP_EDGE",EDGE,{"disambiguationData":[OSD([subQ1,subQ0]),TDD([makeQuery(id+"F6.imprint","IMPRINT",EDGE,{"derivedFrom":makeQuery(id+"F5.boolean.opBoolean","COPY",EDGE,{"derivedFrom":makeQuery(id+"F5.opExtrude","CAP_EDGE",EDGE,{"disambiguationData":[OSD([subQ1,subQ0]),TDD([makeQuery(id+"F4.imprint","IMPRINT",EDGE,{"disambiguationData":[TD([[makeQuery(id+"F4.imprint","INTERSECT",VERTEX,{"derivedFrom":[subQ2,sQuery(id+"F4.wireOp",EDGE,"E4.top"),sQuery(id+"F4.wireOp",EDGE,"E4.right")]}),-1.0]])],"derivedFrom":subQ2})])],"isStart":false})})})])],"isStart":false})});}
            var Q31;
            {var subQ0=sQuery(id+"F0.wireOp",EDGE,"E0.bottom");var subQ1=sQuery(id+"F0.wireOp",EDGE,"E0.right");Q31=makeQuery(id+"F5.boolean.opBoolean","SPLIT",EDGE,{"disambiguationData":[TD([makeQuery(id+"F5.opExtrude","SWEPT_FACE",FACE,{"disambiguationData":[OSD([sQuery(id+"F4.wireOp",EDGE,"E5.left")])]})])],"derivedFrom":makeQuery(id+"F1.opExtrude","SWEPT_EDGE",EDGE,{"disambiguationData":[OSD([subQ0,subQ1])]})});}
            var Q32;
            {var subQ0=sQuery(id+"F0.wireOp",EDGE,"E0.right");var subQ1=sQuery(id+"F0.wireOp",EDGE,"E0.bottom");var subQ2=makeQuery(id+"F1.opExtrude","SWEPT_EDGE",EDGE,{"disambiguationData":[OSD([subQ1,subQ0])]});Q32=makeQuery(id+"F7.boolean.opBoolean","COPY",EDGE,{"derivedFrom":makeQuery(id+"F7.opExtrude","CAP_EDGE",EDGE,{"disambiguationData":[OSD([subQ1,subQ0]),TDD([makeQuery(id+"F6.imprint","IMPRINT",EDGE,{"derivedFrom":makeQuery(id+"F5.boolean.opBoolean","COPY",EDGE,{"derivedFrom":makeQuery(id+"F5.opExtrude","CAP_EDGE",EDGE,{"disambiguationData":[OSD([subQ1,subQ0]),TDD([makeQuery(id+"F4.imprint","IMPRINT",EDGE,{"disambiguationData":[TD([[makeQuery(id+"F4.imprint","INTERSECT",VERTEX,{"derivedFrom":[subQ2,sQuery(id+"F4.wireOp",EDGE,"E5.top"),sQuery(id+"F4.wireOp",EDGE,"E5.right")]}),-1.0]])],"derivedFrom":subQ2})])],"isStart":false})})})])],"isStart":false})});}
            var Q33;
            {var subQ0=sQuery(id+"F0.wireOp",EDGE,"E0.bottom");var subQ1=sQuery(id+"F0.wireOp",EDGE,"E0.right");Q33=makeQuery(id+"F5.boolean.opBoolean","SPLIT",EDGE,{"disambiguationData":[TD([makeQuery(id+"F5.opExtrude","SWEPT_FACE",FACE,{"disambiguationData":[OSD([sQuery(id+"F4.wireOp",EDGE,"E9.trimOffspring")])]})])],"derivedFrom":makeQuery(id+"F1.opExtrude","SWEPT_EDGE",EDGE,{"disambiguationData":[OSD([subQ0,subQ1])]})});}
            var Q34;
            {var subQ0=sQuery(id+"F0.wireOp",EDGE,"E0.right");var subQ1=sQuery(id+"F0.wireOp",EDGE,"E0.bottom");var subQ2=makeQuery(id+"F1.opExtrude","SWEPT_EDGE",EDGE,{"disambiguationData":[OSD([subQ1,subQ0])]});Q34=makeQuery(id+"F7.boolean.opBoolean","COPY",EDGE,{"derivedFrom":makeQuery(id+"F7.opExtrude","CAP_EDGE",EDGE,{"disambiguationData":[OSD([subQ1,subQ0]),TDD([makeQuery(id+"F6.imprint","IMPRINT",EDGE,{"derivedFrom":makeQuery(id+"F5.boolean.opBoolean","COPY",EDGE,{"derivedFrom":makeQuery(id+"F5.opExtrude","CAP_EDGE",EDGE,{"disambiguationData":[OSD([subQ1,subQ0]),TDD([makeQuery(id+"F4.imprint","IMPRINT",EDGE,{"disambiguationData":[TD([[makeQuery(id+"F4.imprint","INTERSECT",VERTEX,{"derivedFrom":[subQ2,sQuery(id+"F4.wireOp",EDGE,"E3")]}),1.0]])],"derivedFrom":subQ2})])],"isStart":false})})})])],"isStart":false})});}
            var Q35;
            {var subQ0=sQuery(id+"F0.wireOp",EDGE,"E0.bottom");var subQ1=sQuery(id+"F0.wireOp",EDGE,"E0.right");Q35=makeQuery(id+"F5.boolean.opBoolean","SPLIT",EDGE,{"disambiguationData":[TD([makeQuery(id+"F5.opExtrude","SWEPT_FACE",FACE,{"disambiguationData":[OSD([sQuery(id+"F4.wireOp",EDGE,"E3")])]})])],"derivedFrom":makeQuery(id+"F1.opExtrude","SWEPT_EDGE",EDGE,{"disambiguationData":[OSD([subQ0,subQ1])]})});}
            fillet(context, id + "F12", {"entities" : qUnion([Q0, Q1, Q2, Q3, Q4, Q5, Q6, Q7, Q8, Q9, Q10, Q11, Q12, Q13, Q14, Q15, Q16, Q17, Q18, Q19, Q20, Q21, Q22, Q23, Q24, Q25, Q26, Q27, Q28, Q29, Q30, Q31, Q32, Q33, Q34, Q35]), "radius" : 0.1 * mm, "tangentPropagation" : true, "allowEdgeOverflow" : false});
        }
        {
            var Q0;
            Q0=makeQuery(id+"F1.opExtrude","CAP_FACE",FACE,{"disambiguationData":[OSD([sQuery(id+"F0.wireOp",EDGE,"E0.bottom"),sQuery(id+"F0.wireOp",EDGE,"E0.top"),sQuery(id+"F0.wireOp",EDGE,"E0.left"),sQuery(id+"F0.wireOp",EDGE,"E0.right")])],"isStart":true});
            var Q1;
            Q1=makeQuery(id+"F1.opExtrude","CAP_FACE",FACE,{"disambiguationData":[OSD([sQuery(id+"F0.wireOp",EDGE,"E0.bottom"),sQuery(id+"F0.wireOp",EDGE,"E0.top"),sQuery(id+"F0.wireOp",EDGE,"E0.left"),sQuery(id+"F0.wireOp",EDGE,"E0.right")])],"isStart":false});
            fillet(context, id + "F13", {"entities" : qUnion([Q0, Q1]), "radius" : 0.3 * mm, "tangentPropagation" : true, "allowEdgeOverflow" : false});
        }
        {
            var Q0;
            {var subQ1=sQuery(id+"F0.wireOp",EDGE,"E0.right");Q0=makeQuery(id+"F5.boolean.opBoolean","SPLIT",FACE,{"disambiguationData":[TD([makeQuery(id+"F5.opExtrude","SWEPT_FACE",FACE,{"disambiguationData":[OSD([sQuery(id+"F4.wireOp",EDGE,"E3")])]})])],"derivedFrom":makeQuery(id+"F1.opExtrude","SWEPT_FACE",FACE,{"disambiguationData":[OSD([subQ1])]})});}
            var Q1;
            Q1=makeQuery(id+"F5.boolean.opBoolean","SPLIT",FACE,{"disambiguationData":[TD([makeQuery(id+"F5.opExtrude","SWEPT_FACE",FACE,{"disambiguationData":[OSD([sQuery(id+"F4.wireOp",EDGE,"E6.left")])]})])],"derivedFrom":makeQuery(id+"F1.opExtrude","SWEPT_FACE",FACE,{"disambiguationData":[OSD([sQuery(id+"F0.wireOp",EDGE,"E0.right")])]})});
            var Q2;
            Q2=makeQuery(id+"F5.boolean.opBoolean","SPLIT",FACE,{"disambiguationData":[TD([makeQuery(id+"F5.opExtrude","SWEPT_FACE",FACE,{"disambiguationData":[OSD([sQuery(id+"F4.wireOp",EDGE,"E7")])]})])],"derivedFrom":makeQuery(id+"F1.opExtrude","SWEPT_FACE",FACE,{"disambiguationData":[OSD([sQuery(id+"F0.wireOp",EDGE,"E0.right")])]})});
            var Q3;
            Q3=makeQuery(id+"F5.boolean.opBoolean","SPLIT",FACE,{"disambiguationData":[TD([makeQuery(id+"F5.opExtrude","SWEPT_FACE",FACE,{"disambiguationData":[OSD([sQuery(id+"F4.wireOp",EDGE,"E5.left")])]})])],"derivedFrom":makeQuery(id+"F1.opExtrude","SWEPT_FACE",FACE,{"disambiguationData":[OSD([sQuery(id+"F0.wireOp",EDGE,"E0.right")])]})});
            var Q4;
            Q4=makeQuery(id+"F5.boolean.opBoolean","SPLIT",FACE,{"disambiguationData":[TD([makeQuery(id+"F5.opExtrude","SWEPT_FACE",FACE,{"disambiguationData":[OSD([sQuery(id+"F4.wireOp",EDGE,"E4.left")])]})])],"derivedFrom":makeQuery(id+"F1.opExtrude","SWEPT_FACE",FACE,{"disambiguationData":[OSD([sQuery(id+"F0.wireOp",EDGE,"E0.right")])]})});
            var Q5;
            {var subQ1=sQuery(id+"F0.wireOp",EDGE,"E0.right");Q5=makeQuery(id+"F5.boolean.opBoolean","SPLIT",FACE,{"disambiguationData":[TD([makeQuery(id+"F5.opExtrude","SWEPT_FACE",FACE,{"disambiguationData":[OSD([sQuery(id+"F4.wireOp",EDGE,"E2")])]})])],"derivedFrom":makeQuery(id+"F1.opExtrude","SWEPT_FACE",FACE,{"disambiguationData":[OSD([subQ1])]})});}
            var Q6;
            Q6=makeQuery(id+"F7.boolean.opBoolean","SPLIT",FACE,{"disambiguationData":[TD([makeQuery(id+"F5.boolean.opBoolean","COPY",FACE,{"derivedFrom":makeQuery(id+"F5.opExtrude","SWEPT_FACE",FACE,{"disambiguationData":[OSD([sQuery(id+"F4.wireOp",EDGE,"E9.trimOffspring")])]})})])],"derivedFrom":makeQuery(id+"F1.opExtrude","SWEPT_FACE",FACE,{"disambiguationData":[OSD([sQuery(id+"F0.wireOp",EDGE,"E0.bottom")])]})});
            var Q7;
            Q7=makeQuery(id+"F7.boolean.opBoolean","SPLIT",FACE,{"disambiguationData":[TD([makeQuery(id+"F7.opExtrude","SWEPT_FACE",FACE,{"disambiguationData":[OSD([sQuery(id+"F6.wireOp",EDGE,"E16")])]})])],"derivedFrom":makeQuery(id+"F1.opExtrude","SWEPT_FACE",FACE,{"disambiguationData":[OSD([sQuery(id+"F0.wireOp",EDGE,"E0.bottom")])]})});
            var Q8;
            Q8=makeQuery(id+"F9.boolean.opBoolean","SPLIT",FACE,{"disambiguationData":[TD([makeQuery(id+"F7.boolean.opBoolean","COPY",FACE,{"derivedFrom":makeQuery(id+"F7.opExtrude","SWEPT_FACE",FACE,{"disambiguationData":[OSD([sQuery(id+"F6.wireOp",EDGE,"E18.trimOffspring")])]})})])],"derivedFrom":makeQuery(id+"F1.opExtrude","SWEPT_FACE",FACE,{"disambiguationData":[OSD([sQuery(id+"F0.wireOp",EDGE,"E0.left")])]})});
            var Q9;
            Q9=makeQuery(id+"F9.boolean.opBoolean","SPLIT",FACE,{"disambiguationData":[TD([makeQuery(id+"F9.opExtrude","SWEPT_FACE",FACE,{"disambiguationData":[OSD([sQuery(id+"F8.wireOp",EDGE,"E25")])]})])],"derivedFrom":makeQuery(id+"F1.opExtrude","SWEPT_FACE",FACE,{"disambiguationData":[OSD([sQuery(id+"F0.wireOp",EDGE,"E0.left")])]})});
            var Q10;
            Q10=makeQuery(id+"F11.boolean.opBoolean","SPLIT",FACE,{"disambiguationData":[TD([makeQuery(id+"F9.boolean.opBoolean","COPY",FACE,{"derivedFrom":makeQuery(id+"F9.opExtrude","SWEPT_FACE",FACE,{"disambiguationData":[OSD([sQuery(id+"F8.wireOp",EDGE,"E27.trimOffspring")])]})})])],"derivedFrom":makeQuery(id+"F1.opExtrude","SWEPT_FACE",FACE,{"disambiguationData":[OSD([sQuery(id+"F0.wireOp",EDGE,"E0.top")])]})});
            var Q11;
            Q11=makeQuery(id+"F11.boolean.opBoolean","SPLIT",FACE,{"disambiguationData":[TD([makeQuery(id+"F5.boolean.opBoolean","COPY",FACE,{"derivedFrom":makeQuery(id+"F5.opExtrude","SWEPT_FACE",FACE,{"disambiguationData":[OSD([sQuery(id+"F4.wireOp",EDGE,"E6.left")])]})})])],"derivedFrom":makeQuery(id+"F1.opExtrude","SWEPT_FACE",FACE,{"disambiguationData":[OSD([sQuery(id+"F0.wireOp",EDGE,"E0.top")])]})});
            fillet(context, id + "F14", {"entities" : qUnion([Q0, Q1, Q2, Q3, Q4, Q5, Q6, Q7, Q8, Q9, Q10, Q11]), "radius" : 0.1 * mm, "tangentPropagation" : true, "allowEdgeOverflow" : false});
        }
    });
